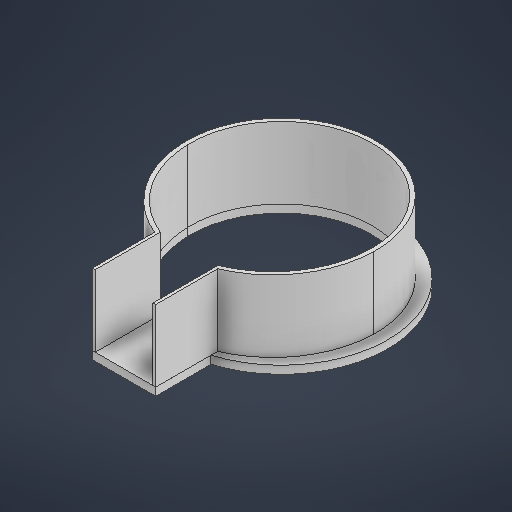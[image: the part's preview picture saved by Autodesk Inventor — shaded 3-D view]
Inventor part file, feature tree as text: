
AUTODESK INVENTOR PART (.ipt)
format: ipt  version: 2025 (Build 290162000, 162)  size: 256,000 bytes
history: native  units: in
note: dims shown in document units (in); Inventor stores cm internally (conversion verified against a paired STEP export)
features: extrude x2, sketch x2
ambient origin geometry x8: Origin, YZ Plane, XZ Plane, XY Plane, X Axis, Y Axis, Z Axis, Center Point
bodies: Solid1 (feature_tree)
feature tree (4):
  extrude  "Extrusion1"  Depth=0.3937in TaperAngle=0.0deg
  extrude  "Extrusion2"  Depth=3.1496in
  sketch  "Sketch1"  dims[d0=10.6299in d2=0.3937in d3=0.0in]
  sketch  "Sketch2"  dims[d4=0.1919in d7=3.1496in d9=9.0551in d13=2.7559in d15=0.1969in d16=0.1378in d17=0.1969in d18=3.563in d19=0.0in d5=0.0197in d6=0.0344in d8=0.0344in d10=0.0344in]
